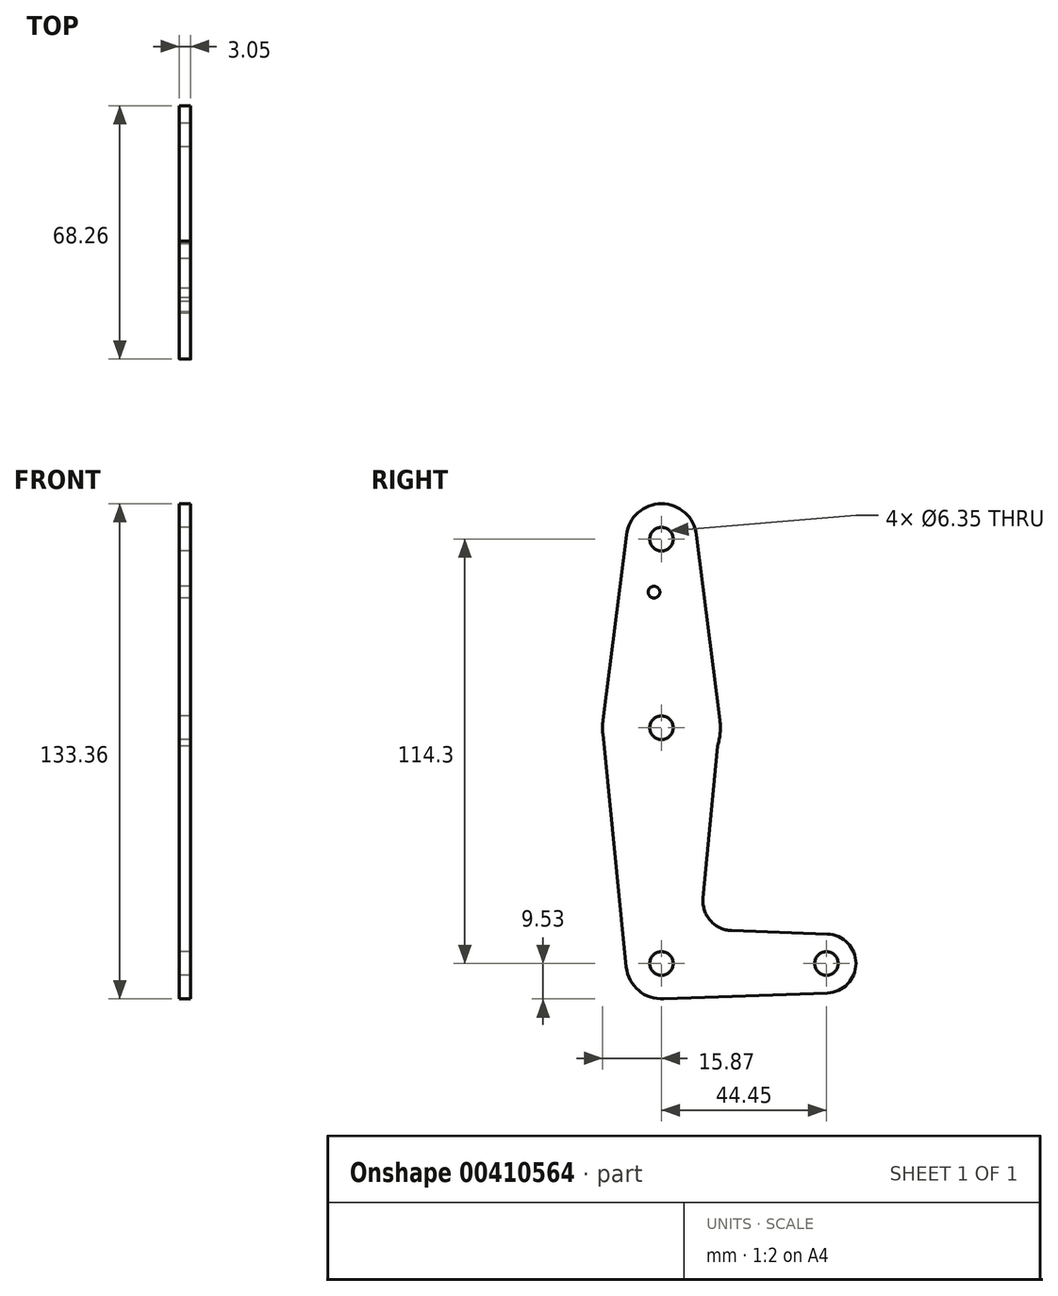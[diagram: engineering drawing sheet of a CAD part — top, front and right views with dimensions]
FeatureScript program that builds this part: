
annotation { "Feature Type Name" : "Feature", "Feature Type Description" : "" }
export const myFeature = defineFeature(function(context is Context, id is Id, definition is map)
    precondition{}
    {
        {
            var Q0;
            Q0=qCreatedBy(makeId("Right.planeOp"),FACE);
            var sketch = newSketch(context, id + "F0", { "sketchPlane" : qUnion([Q0])});
            skCircle(sketch, "E0", {"center": v(0, 0) * mm, "radius": 9.53 * mm});
            skCircle(sketch, "E1", {"center": v(0, 63.5) * mm, "radius": 15.88 * mm});
            skCircle(sketch, "E2", {"center": v(0, 114.3) * mm, "radius": 9.53 * mm});
            skCircle(sketch, "E3", {"center": v(44.45, 0) * mm, "radius": 7.94 * mm});
            skLineSegment(sketch, "E4", {"start": v(0, 114.3) * mm, "end": v(0, 0) * mm});
            skLineSegment(sketch, "E5", {"start": v(0, 0) * mm, "end": v(44.45, 0) * mm});
            skLineSegment(sketch, "E6", {"start": v(9.45, 115.5) * mm, "end": v(15.75, 65.48) * mm});
            skLineSegment(sketch, "E7", {"start": v(18.86, 8.85) * mm, "end": v(44.73, 7.93) * mm});
            skLineSegment(sketch, "E8", {"start": v(0, -9.53) * mm, "end": v(44.73, -7.93) * mm});
            skCircle(sketch, "E9", {"center": v(0, 114.3) * mm, "radius": 3.18 * mm});
            skCircle(sketch, "E10", {"center": v(-2.01, 100.03) * mm, "radius": 1.59 * mm});
            skCircle(sketch, "E11", {"center": v(0, 0) * mm, "radius": 3.18 * mm});
            skCircle(sketch, "E12", {"center": v(0, 63.5) * mm, "radius": 3.18 * mm});
            skCircle(sketch, "E13", {"center": v(44.45, 0) * mm, "radius": 3.18 * mm});
            skPoint(sketch, "E14.newPointB", {"position": v(9.57, 0) * mm});
            skArc(sketch, "E14.filletArc", {"start": v(11.22, 17.55) * mm, "mid": v(13.16, 11.55) * mm, "end": v(18.86, 8.85) * mm});
            skLineSegment(sketch, "E15", {"start": v(11.22, 17.55) * mm, "end": v(15.1, 58.6) * mm});
            skLineSegment(sketch, "E16", {"start": v(-9.48, -0.95) * mm, "end": v(-15.8, 61.91) * mm});
            skLineSegment(sketch, "E17", {"start": v(-9.45, 115.5) * mm, "end": v(-15.75, 65.48) * mm});
            skSolve(sketch);
        }
        {
            var Q0;
            {var subQ1=sQuery(id+"F0.wireOp",EDGE,"E1");var subQ6=makeQuery(id+"F0.imprint","INTERSECT",VERTEX,{"derivedFrom":[subQ1,sQuery(id+"F0.wireOp",EDGE,"E17")]});Q0=makeQuery(id+"F0.imprint","IMPRINT",FACE,{"disambiguationData":[TD([[makeQuery(id+"F0.imprint","IMPRINT",EDGE,{"disambiguationData":[TD([[subQ6,1.0]])],"derivedFrom":subQ1}),1.0]])]});}
            var Q1;
            Q1 = qSketchRegion(id + "F0", true);
            var Q2;
            {var subQ0=sQuery(id+"F0.wireOp",EDGE,"E4");var subQ1=sQuery(id+"F0.wireOp",EDGE,"E0");var subQ2=makeQuery(id+"F0.imprint","INTERSECT",VERTEX,{"derivedFrom":[subQ1,subQ0]});Q2=makeQuery(id+"F0.imprint","IMPRINT",FACE,{"disambiguationData":[TD([[makeQuery(id+"F0.imprint","IMPRINT",EDGE,{"disambiguationData":[TD([[subQ2,1.0]])],"derivedFrom":subQ1}),1.0]])]});}
            extrude(context, id + "F1", {"entities" : qUnion([Q0, Q1, Q2]), "depth" : 3.05 * mm});
        }
    });
